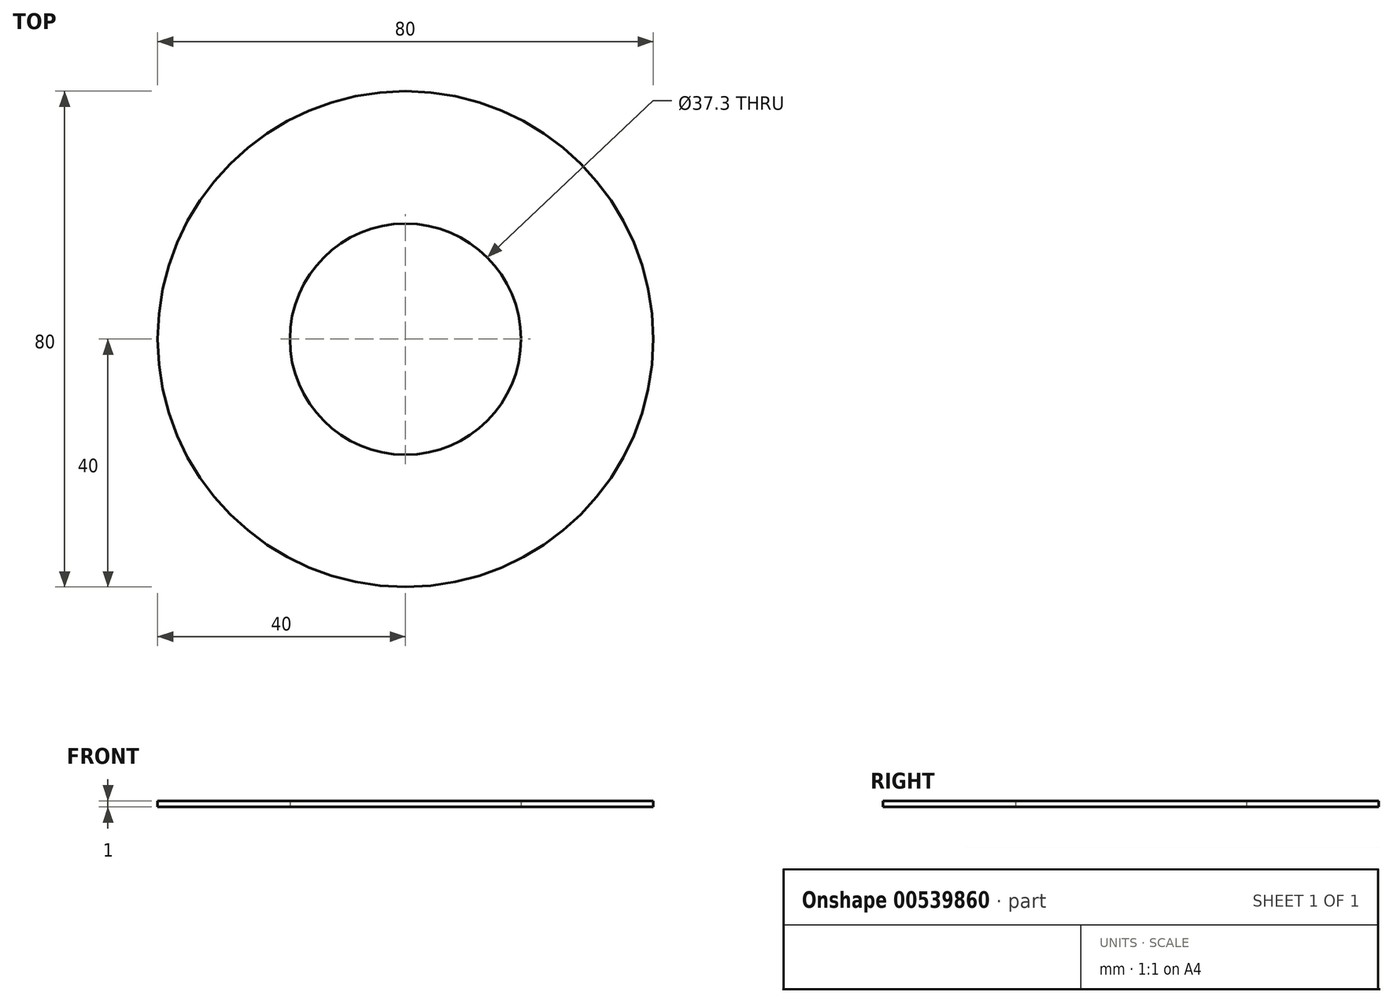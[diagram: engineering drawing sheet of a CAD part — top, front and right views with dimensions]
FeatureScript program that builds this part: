
annotation { "Feature Type Name" : "Feature", "Feature Type Description" : "" }
export const myFeature = defineFeature(function(context is Context, id is Id, definition is map)
    precondition{}
    {
        {
            var Q0;
            Q0=qCreatedBy(makeId("Top.planeOp"),FACE);
            var sketch = newSketch(context, id + "F0", { "sketchPlane" : qUnion([Q0])});
            skCircle(sketch, "E0", {"center": v(0, 0) * mm, "radius": 18.65 * mm});
            skCircle(sketch, "E1", {"center": v(0, 0) * mm, "radius": 40 * mm});
            skSolve(sketch);
        }
        {
            var Q0;
            Q0 = qSketchRegion(id + "F0", true);
            extrude(context, id + "F1", {"entities" : qUnion([Q0]), "depth" : 1 * mm, "offsetDistance" : 25 * mm});
        }
    });
